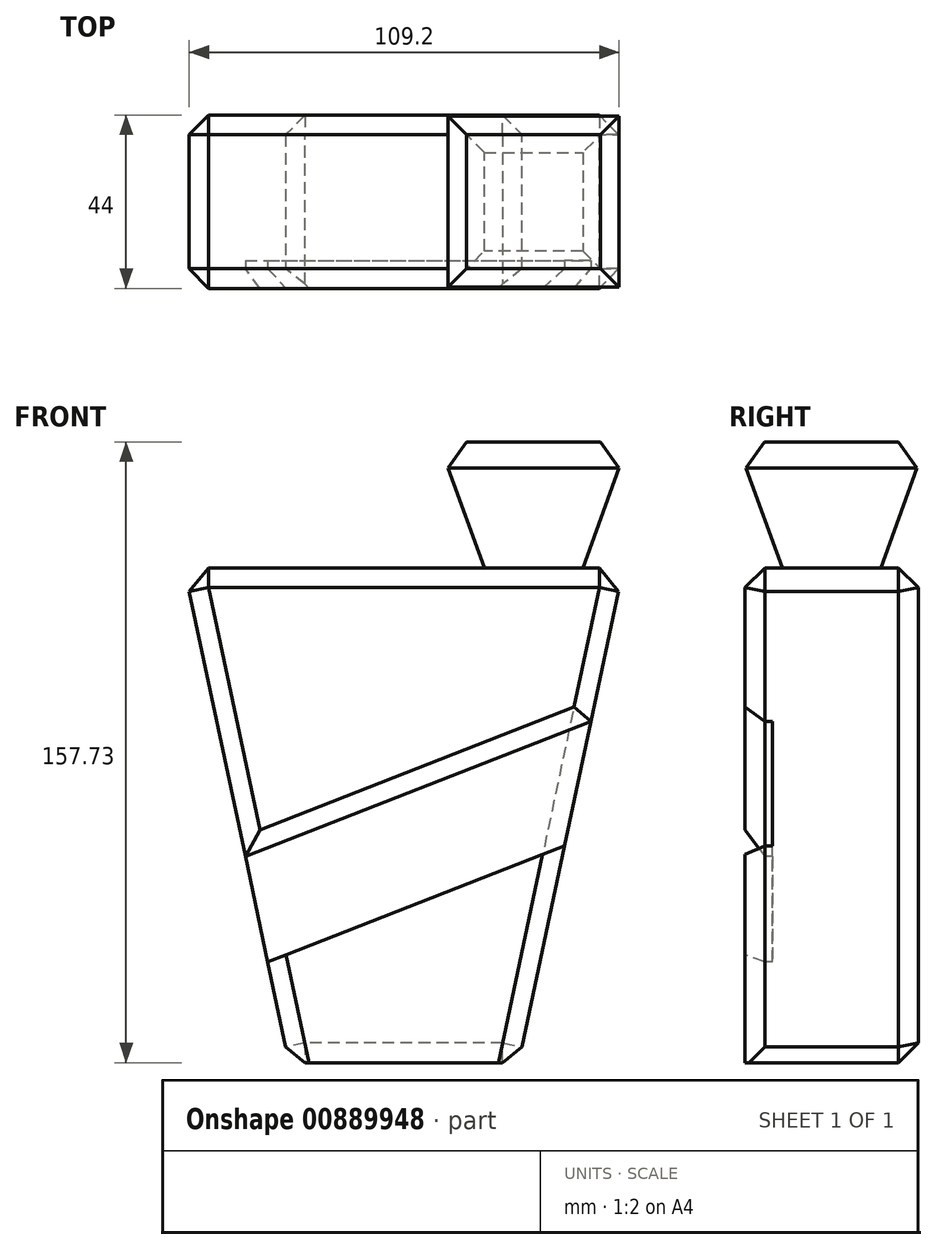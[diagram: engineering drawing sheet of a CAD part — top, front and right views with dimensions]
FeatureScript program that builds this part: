
annotation { "Feature Type Name" : "Feature", "Feature Type Description" : "" }
export const myFeature = defineFeature(function(context is Context, id is Id, definition is map)
    precondition{}
    {
        {
            var Q0;
            Q0=qCreatedBy(makeId("Front.planeOp"),FACE);
            var sketch = newSketch(context, id + "F0", { "sketchPlane" : qUnion([Q0])});
            skLineSegment(sketch, "E0", {"start": v(0, 0) * mm, "end": v(55.81, 0) * mm});
            skLineSegment(sketch, "E1", {"start": v(55.81, 0) * mm, "end": v(29.17, -125.73) * mm});
            skLineSegment(sketch, "E2", {"start": v(29.17, -125.73) * mm, "end": v(0, -125.73) * mm});
            skLineSegment(sketch, "E3", {"start": v(0, -125.73) * mm, "end": v(0, 0) * mm});
            skLineSegment(sketch, "E4.MirrorCS", {"start": v(0, 0) * mm, "end": v(-55.81, 0) * mm});
            skLineSegment(sketch, "E5.MirrorCS", {"start": v(-55.81, 0) * mm, "end": v(-29.17, -125.73) * mm});
            skLineSegment(sketch, "E6.MirrorCS", {"start": v(-29.17, -125.73) * mm, "end": v(0, -125.73) * mm});
            skSolve(sketch);
        }
        {
            var Q0;
            Q0=makeQuery(id+"F0.imprint","IMPRINT",FACE,{"disambiguationData":[TD([[makeQuery(id+"F0.imprint","IMPRINT",EDGE,{"derivedFrom":sQuery(id+"F0.wireOp",EDGE,"E0")}),-1.0]])]});
            var Q1;
            Q1=makeQuery(id+"F0.imprint","IMPRINT",FACE,{"disambiguationData":[TD([[makeQuery(id+"F0.imprint","IMPRINT",EDGE,{"derivedFrom":sQuery(id+"F0.wireOp",EDGE,"E3")}),1.0]])]});
            extrude(context, id + "F1", {"entities" : qUnion([Q0, Q1]), "endBound" : BoundingType.SYMMETRIC, "depth" : 44 * mm, "offsetDistance" : 25 * mm});
        }
        {
            var Q0;
            Q0=makeQuery(id+"F1.opExtrude","SWEPT_FACE",FACE,{"disambiguationData":[OSD([sQuery(id+"F0.wireOp",EDGE,"E0"),sQuery(id+"F0.wireOp",EDGE,"E4.MirrorCS")])]});
            var sketch = newSketch(context, id + "F2", { "sketchPlane" : qUnion([Q0])});
            skLineSegment(sketch, "E7.bottom", {"start": v(45.47, -12.5) * mm, "end": v(20.47, -12.5) * mm});
            skLineSegment(sketch, "E7.top", {"start": v(45.47, 12.5) * mm, "end": v(20.47, 12.5) * mm});
            skLineSegment(sketch, "E7.left", {"start": v(45.47, -12.5) * mm, "end": v(45.47, 12.5) * mm});
            skLineSegment(sketch, "E7.right", {"start": v(20.47, -12.5) * mm, "end": v(20.47, 12.5) * mm});
            skPoint(sketch, "E7.middle", {"position": v(32.97, 0) * mm});
            skSolve(sketch);
        }
        {
            var Q0;
            Q0=makeQuery(id+"F2.imprint","IMPRINT",FACE,{"disambiguationData":[TD([[makeQuery(id+"F2.imprint","IMPRINT",EDGE,{"derivedFrom":sQuery(id+"F2.wireOp",EDGE,"E7.bottom")}),-1.0]])]});
            extrude(context, id + "F3", {"entities" : qUnion([Q0]), "depth" : 32 * mm, "offsetDistance" : 25 * mm, "hasDraft" : true, "draftAngle" : 20 * degree});
        }
        {
            var Q0;
            Q0=makeQuery(id+"F1.opExtrude","CAP_FACE",FACE,{"disambiguationData":[OSD([sQuery(id+"F0.wireOp",EDGE,"E0"),sQuery(id+"F0.wireOp",EDGE,"E1"),sQuery(id+"F0.wireOp",EDGE,"E2"),sQuery(id+"F0.wireOp",EDGE,"E4.MirrorCS"),sQuery(id+"F0.wireOp",EDGE,"E5.MirrorCS"),sQuery(id+"F0.wireOp",EDGE,"E6.MirrorCS")])],"isStart":false});
            var sketch = newSketch(context, id + "F4", { "sketchPlane" : qUnion([Q0])});
            skSolve(sketch);
        }
        {
            var Q0;
            Q0=makeQuery(id+"F4.imprint","IMPRINT",FACE,{"disambiguationData":[TD([[makeQuery(id+"F4.imprint","IMPRINT",EDGE,{"derivedFrom":makeQuery(id+"F1.opExtrude","CAP_EDGE",EDGE,{"disambiguationData":[OSD([sQuery(id+"F0.wireOp",EDGE,"E1")])],"isStart":false})}),-1.0]])]});
            var sketch = newSketch(context, id + "F5", { "sketchPlane" : qUnion([Q0])});
            skLineSegment(sketch, "E8", {"start": v(-79.82, -88.85) * mm, "end": v(73.8, -28.78) * mm});
            skLineSegment(sketch, "E9.0", {"start": v(-69.98, -114) * mm, "end": v(83.63, -53.93) * mm});
            skLineSegment(sketch, "E10", {"start": v(-79.82, -88.85) * mm, "end": v(-69.98, -114) * mm});
            skLineSegment(sketch, "E11", {"start": v(83.63, -53.93) * mm, "end": v(73.8, -28.78) * mm});
            skSolve(sketch);
        }
        {
            var Q0;
            {var subQ0=sQuery(id+"F5.wireOp",EDGE,"E8");var subQ1=makeQuery(id+"F4.imprint","IMPRINT",EDGE,{"derivedFrom":makeQuery(id+"F1.opExtrude","CAP_EDGE",EDGE,{"disambiguationData":[OSD([sQuery(id+"F0.wireOp",EDGE,"E5.MirrorCS")])],"isStart":false})});var subQ2=makeQuery(id+"F5.imprint","INTERSECT",VERTEX,{"derivedFrom":[subQ1,subQ0]});Q0=makeQuery(id+"F5.imprint","IMPRINT",FACE,{"disambiguationData":[TD([[makeQuery(id+"F5.imprint","IMPRINT",EDGE,{"disambiguationData":[TD([[subQ2,-1.0]])],"derivedFrom":subQ0}),-1.0]])]});}
            extrude(context, id + "F6", {"entities" : qUnion([Q0]), "operationType" : NewBodyOperationType.ADD, "oppositeDirection" : true, "depth" : 4 * mm, "offsetDistance" : 25 * mm, "hasDraft" : true, "draftAngle" : 3 * degree, "draftPullDirection" : true});
        }
        {
            var Q0;
            {var subQ0=sQuery(id+"F5.wireOp",EDGE,"E8");var subQ1=makeQuery(id+"F4.imprint","IMPRINT",EDGE,{"derivedFrom":makeQuery(id+"F1.opExtrude","CAP_EDGE",EDGE,{"disambiguationData":[OSD([sQuery(id+"F0.wireOp",EDGE,"E5.MirrorCS")])],"isStart":false})});var subQ2=makeQuery(id+"F5.imprint","INTERSECT",VERTEX,{"derivedFrom":[subQ1,subQ0]});Q0=makeQuery(id+"F5.imprint","IMPRINT",FACE,{"disambiguationData":[TD([[makeQuery(id+"F5.imprint","IMPRINT",EDGE,{"disambiguationData":[TD([[subQ2,-1.0]])],"derivedFrom":subQ0}),-1.0]])]});}
            extrude(context, id + "F7", {"entities" : qUnion([Q0]), "operationType" : NewBodyOperationType.REMOVE, "oppositeDirection" : true, "depth" : 7 * mm, "offsetDistance" : 25 * mm});
        }
        {
            var Q0;
            Q0=makeQuery(id+"F1.opExtrude","SWEPT_EDGE",EDGE,{"disambiguationData":[OSD([sQuery(id+"F0.wireOp",EDGE,"E4.MirrorCS"),sQuery(id+"F0.wireOp",EDGE,"E5.MirrorCS")])]});
            var Q1;
            {var subQ0=sQuery(id+"F0.wireOp",EDGE,"E5.MirrorCS");Q1=makeQuery(id+"F7.boolean.opBoolean","SPLIT",EDGE,{"disambiguationData":[TD([makeQuery(id+"F7.opExtrude","SWEPT_FACE",FACE,{"disambiguationData":[OSD([sQuery(id+"F5.wireOp",EDGE,"E8")])]})])],"derivedFrom":makeQuery(id+"F1.opExtrude","CAP_EDGE",EDGE,{"disambiguationData":[OSD([subQ0])],"isStart":false})});}
            var Q2;
            {var subQ1=sQuery(id+"F0.wireOp",EDGE,"E5.MirrorCS");Q2=makeQuery(id+"F7.boolean.opBoolean","SPLIT",EDGE,{"disambiguationData":[TD([makeQuery(id+"F7.opExtrude","SWEPT_FACE",FACE,{"disambiguationData":[OSD([sQuery(id+"F5.wireOp",EDGE,"E9.0")])]})])],"derivedFrom":makeQuery(id+"F1.opExtrude","CAP_EDGE",EDGE,{"disambiguationData":[OSD([subQ1])],"isStart":false})});}
            var Q3;
            {var subQ2=sQuery(id+"F0.wireOp",EDGE,"E1");Q3=makeQuery(id+"F7.boolean.opBoolean","SPLIT",EDGE,{"disambiguationData":[TD([makeQuery(id+"F7.opExtrude","SWEPT_FACE",FACE,{"disambiguationData":[OSD([sQuery(id+"F5.wireOp",EDGE,"E9.0")])]})])],"derivedFrom":makeQuery(id+"F1.opExtrude","CAP_EDGE",EDGE,{"disambiguationData":[OSD([subQ2])],"isStart":false})});}
            var Q4;
            {var subQ1=sQuery(id+"F0.wireOp",EDGE,"E1");Q4=makeQuery(id+"F7.boolean.opBoolean","SPLIT",EDGE,{"disambiguationData":[TD([makeQuery(id+"F7.opExtrude","SWEPT_FACE",FACE,{"disambiguationData":[OSD([sQuery(id+"F5.wireOp",EDGE,"E8")])]})])],"derivedFrom":makeQuery(id+"F1.opExtrude","CAP_EDGE",EDGE,{"disambiguationData":[OSD([subQ1])],"isStart":false})});}
            var Q5;
            Q5=makeQuery(id+"F1.opExtrude","CAP_EDGE",EDGE,{"disambiguationData":[OSD([sQuery(id+"F0.wireOp",EDGE,"E0"),sQuery(id+"F0.wireOp",EDGE,"E4.MirrorCS")])],"isStart":false});
            var Q6;
            Q6=makeQuery(id+"F1.opExtrude","CAP_EDGE",EDGE,{"disambiguationData":[OSD([sQuery(id+"F0.wireOp",EDGE,"E0"),sQuery(id+"F0.wireOp",EDGE,"E4.MirrorCS")])],"isStart":true});
            var Q7;
            Q7=makeQuery(id+"F1.opExtrude","CAP_EDGE",EDGE,{"disambiguationData":[OSD([sQuery(id+"F0.wireOp",EDGE,"E5.MirrorCS")])],"isStart":true});
            var Q8;
            Q8=makeQuery(id+"F1.opExtrude","CAP_EDGE",EDGE,{"disambiguationData":[OSD([sQuery(id+"F0.wireOp",EDGE,"E1")])],"isStart":true});
            var Q9;
            Q9=makeQuery(id+"F1.opExtrude","CAP_EDGE",EDGE,{"disambiguationData":[OSD([sQuery(id+"F0.wireOp",EDGE,"E2"),sQuery(id+"F0.wireOp",EDGE,"E6.MirrorCS")])],"isStart":true});
            var Q10;
            Q10=makeQuery(id+"F1.opExtrude","SWEPT_EDGE",EDGE,{"disambiguationData":[OSD([sQuery(id+"F0.wireOp",EDGE,"E5.MirrorCS"),sQuery(id+"F0.wireOp",EDGE,"E6.MirrorCS")])]});
            var Q11;
            Q11=makeQuery(id+"F1.opExtrude","SWEPT_EDGE",EDGE,{"disambiguationData":[OSD([sQuery(id+"F0.wireOp",EDGE,"E1"),sQuery(id+"F0.wireOp",EDGE,"E2")])]});
            var Q12;
            Q12=makeQuery(id+"F1.opExtrude","SWEPT_EDGE",EDGE,{"disambiguationData":[OSD([sQuery(id+"F0.wireOp",EDGE,"E0"),sQuery(id+"F0.wireOp",EDGE,"E1")])]});
            chamfer(context, id + "F8", {"entities" : qUnion([Q0, Q1, Q2, Q3, Q4, Q5, Q6, Q7, Q8, Q9, Q10, Q11, Q12]), "width" : 5 * mm, "tangentPropagation" : true});
        }
        {
            var Q0;
            Q0=makeQuery(id+"F7.boolean.opBoolean","COPY",EDGE,{"derivedFrom":makeQuery(id+"F7.opExtrude","CAP_EDGE",EDGE,{"disambiguationData":[OSD([sQuery(id+"F5.wireOp",EDGE,"E9.0")])],"isStart":true})});
            var Q1;
            Q1=makeQuery(id+"F7.boolean.opBoolean","COPY",EDGE,{"derivedFrom":makeQuery(id+"F7.opExtrude","CAP_EDGE",EDGE,{"disambiguationData":[OSD([sQuery(id+"F5.wireOp",EDGE,"E8")])],"isStart":true})});
            chamfer(context, id + "F9", {"entities" : qUnion([Q0, Q1]), "width" : 5 * mm, "tangentPropagation" : true});
        }
        {
            var Q0;
            Q0=makeQuery(id+"F3.opExtrude","CAP_EDGE",EDGE,{"disambiguationData":[OSD([sQuery(id+"F2.wireOp",EDGE,"E7.bottom")])],"isStart":false});
            var Q1;
            Q1=makeQuery(id+"F3.opExtrude","CAP_EDGE",EDGE,{"disambiguationData":[OSD([sQuery(id+"F2.wireOp",EDGE,"E7.right")])],"isStart":false});
            var Q2;
            Q2=makeQuery(id+"F3.opExtrude","CAP_EDGE",EDGE,{"disambiguationData":[OSD([sQuery(id+"F2.wireOp",EDGE,"E7.top")])],"isStart":false});
            var Q3;
            Q3=makeQuery(id+"F3.opExtrude","CAP_EDGE",EDGE,{"disambiguationData":[OSD([sQuery(id+"F2.wireOp",EDGE,"E7.left")])],"isStart":false});
            chamfer(context, id + "F10", {"entities" : qUnion([Q0, Q1, Q2, Q3]), "width" : 5 * mm, "tangentPropagation" : true});
        }
    });
